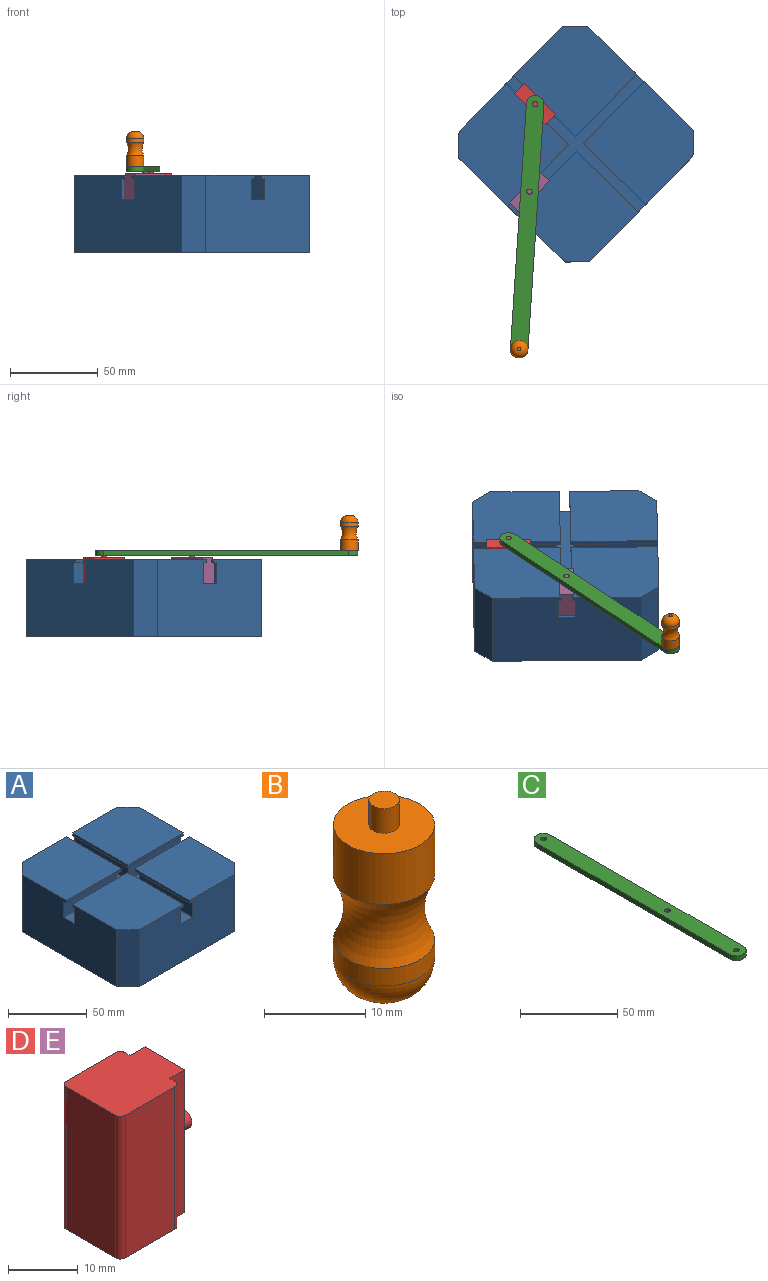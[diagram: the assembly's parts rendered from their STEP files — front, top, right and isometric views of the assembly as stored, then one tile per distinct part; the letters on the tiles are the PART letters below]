
ASSEMBLY  parts=5 mates=5
PART A: 34 faces, bbox 105x105x44 mm
  f0: plane 49.5x49.5mm, normal (0,0,1), area 2400.2mm2, adj f8,f10,f12,f13,f28
  f1: plane 49.5x49.5mm, normal (0,0,1), area 2400.2mm2, adj f4,f5,f10,f11,f33
  f2: plane 49.5x49.5mm, normal (0,0,-1), area 194mm2, adj f4,f5,f6,f10,f31,f33
  f3: plane 49.52x49.5mm, normal (0,0,-1), area 194mm2, adj f13,f15,f23,f25,f26,f29
  f4: plane 85x44mm, normal (1,0,0), area 3608.3mm2, adj f1,f2,f11,f16,f17,f18,f20,f22
  f5: plane 49.5x2mm, normal (-1,0,0), area 99mm2, adj f1,f2,f10,f33
  f6: plane 47.5x12mm, normal (-1,0,0), area 570mm2, adj f2,f10,f22,f31
  f7: plane 47.5x12mm, normal (1,0,0), area 570mm2, adj f10,f22,f24,f27
  f8: plane 49.5x2mm, normal (1,0,0), area 99mm2, adj f0,f10,f24,f28
  f9: plane 49.52x49.5mm, normal (0,0,1), area 2401.5mm2, adj f13,f14,f15,f25,f26
  f10: plane 85x44mm, normal (0,1,0), area 3608mm2, adj f0,f1,f2,f5,f6,f7,f8,f11
  f11: plane 44x10mm, normal (0.71,0.71,0), area 622.3mm2, adj f1,f4,f10,f18
  f12: plane 44x10mm, normal (-0.71,0.71,0), area 622.3mm2, adj f0,f10,f13,f18
  f13: plane 85x44mm, normal (-1,0,0), area 3608.3mm2, adj f0,f3,f9,f12,f14,f18,f22,f24
  f14: plane 44x10mm, normal (-0.71,-0.71,0), area 622.3mm2, adj f9,f13,f15,f18
  f15: plane 85x44mm, normal (0,-1,0), area 3608mm2, adj f3,f9,f14,f16,f17,f18,f19,f20
  f16: plane 44x10mm, normal (0.71,-0.71,0), area 622.3mm2, adj f4,f15,f17,f18
  f17: plane 49.52x49.5mm, normal (0,0,1), area 2401.5mm2, adj f4,f15,f16,f19,f32
  f18: plane 105x105mm, normal (0,0,-1), area 10825mm2, adj f4,f10,f11,f12,f13,f14,f15,f16
  f19: plane 49.52x2mm, normal (-1,0,0), area 99mm2, adj f15,f17,f20,f32
  f20: plane 49.52x49.5mm, normal (0,0,-1), area 194mm2, adj f4,f15,f19,f21,f30,f32
  f21: plane 47.52x12mm, normal (-1,0,0), area 570.3mm2, adj f15,f20,f22,f30
  f22: plane 105x105mm, normal (0,0,1), area 1997.7mm2, adj f4,f6,f7,f10,f13,f15,f21,f23
  f23: plane 47.52x12mm, normal (1,0,0), area 570.3mm2, adj f3,f15,f22,f29
  f24: plane 49.5x49.5mm, normal (0,0,-1), area 194mm2, adj f7,f8,f10,f13,f27,f28
  f25: plane 49.52x2mm, normal (1,0,0), area 99mm2, adj f3,f9,f15,f26
  f26: plane 49.5x2mm, normal (0,1,0), area 99mm2, adj f3,f9,f13,f25
  f27: plane 47.5x12mm, normal (0,-1,0), area 570mm2, adj f7,f13,f22,f24
  f28: plane 49.5x2mm, normal (0,-1,0), area 99mm2, adj f0,f8,f13,f24
  f29: plane 47.5x12mm, normal (0,1,0), area 570mm2, adj f3,f13,f22,f23
  f30: plane 47.5x12mm, normal (0,1,0), area 570mm2, adj f4,f20,f21,f22
  f31: plane 47.5x12mm, normal (0,-1,0), area 570mm2, adj f2,f4,f6,f22
  f32: plane 49.5x2mm, normal (0,1,0), area 99mm2, adj f4,f17,f19,f20
  f33: plane 49.5x2mm, normal (0,-1,0), area 99mm2, adj f1,f2,f4,f5
PART B: 8 faces, bbox 13.7x13.7x23 mm
  f0: plane 2x2mm, normal (0,0,-1), area 3.1mm2, adj f1
  f1: torus R=1mm, axis (0,0,-1), area 140mm2, adj f0,f2
  f2: cylinder r=5mm len=10mm, axis (0,0,-1), area 66.8mm2, adj f1,f3
  f3: torus R=12mm, axis (0,0,-1), area 220.3mm2, adj f2,f4
  f4: cylinder r=5mm len=10mm, axis (0,0,-1), area 192.5mm2, adj f3,f5
  f5: plane 10x10mm, normal (0,0,1), area 71.5mm2, adj f4,f6
  f6: cylinder r=1.5mm len=3mm, axis (0,0,-1), area 28.3mm2, adj f5,f7
  f7: plane 3x3mm, normal (0,0,1), area 7.1mm2, adj f6
PART C: 9 faces, bbox 10x150x3 mm
  f0: cylinder r=5mm len=10mm, axis (0,0,-1), area 47.1mm2, adj f1,f6,f7,f8
  f1: plane 140x3mm, normal (-1,0,0), area 420mm2, adj f0,f2,f7,f8
  f2: cylinder r=5mm len=10mm, axis (0,0,-1), area 47.1mm2, adj f1,f6,f7,f8
  f3: cylinder r=1.5mm len=3mm, axis (0,0,-1), area 28.3mm2, adj f7,f8
  f4: cylinder r=1.5mm len=3mm, axis (0,0,-1), area 28.3mm2, adj f7,f8
  f5: cylinder r=1.5mm len=3mm, axis (0,0,-1), area 28.3mm2, adj f7,f8
  f6: plane 140x3mm, normal (1,0,0), area 420mm2, adj f0,f2,f7,f8
  f7: plane 150x10mm, normal (0,0,1), area 1457.3mm2, adj f0,f1,f2,f3,f4,f5,f6
  f8: plane 150x10mm, normal (0,0,-1), area 1457.3mm2, adj f0,f1,f2,f3,f4,f5,f6
PART D: 16 faces, bbox 19x12x25 mm
  f0: plane 25x1mm, normal (1,0,0), area 25mm2, adj f1,f3,f8,f13
  f1: plane 15x12mm, normal (0,0,-1), area 167.1mm2, adj f0,f2,f4,f5,f6,f7,f8,f9
  f2: plane 25x10mm, normal (0,1,0), area 250mm2, adj f1,f3,f13,f14
  f3: plane 15x12mm, normal (0,0,1), area 167.1mm2, adj f0,f2,f4,f5,f6,f7,f8,f9
  f4: plane 25x10mm, normal (0,-1,0), area 250mm2, adj f1,f3,f12,f15
  f5: plane 25x1mm, normal (1,0,0), area 25mm2, adj f1,f3,f7,f12
  f6: plane 25x10mm, normal (-1,0,0), area 250mm2, adj f1,f3,f14,f15
  f7: plane 25x3mm, normal (0,-1,0), area 75mm2, adj f1,f3,f5,f9
  f8: plane 25x3mm, normal (0,1,0), area 75mm2, adj f0,f1,f3,f9
  f9: plane 25x8mm, normal (1,0,0), area 192.9mm2, adj f1,f3,f7,f8,f10
  f10: cylinder r=1.5mm len=4mm, axis (-1,0,0), area 37.7mm2, adj f9,f11
  f11: plane 3x3mm, normal (1,0,0), area 7.1mm2, adj f10
  f12: cylinder r=1mm len=25mm, axis (0,0,1), area 39.3mm2, adj f1,f3,f4,f5
  f13: cylinder r=1mm len=25mm, axis (0,0,-1), area 39.3mm2, adj f0,f1,f2,f3
  f14: cylinder r=1mm len=25mm, axis (0,0,1), area 39.3mm2, adj f1,f2,f3,f6
  f15: cylinder r=1mm len=25mm, axis (0,0,-1), area 39.3mm2, adj f1,f3,f4,f6
PART E: same geometry as D
PLACE A rot(axis=(0,0,-1),134.3deg) t=(-66.8,1.1,-30)mm fixed
PLACE B rot(axis=(0.68,-0.73,0),180deg) t=(39.52,-119.17,78.07)mm
PLACE C rot(axis=(0,0,1),176.3deg) t=(51.57,20.34,15.92)mm
PLACE D rot(axis=(-0.35,-0.87,-0.35),98.2deg) t=(49.82,74.19,-0.08)mm
PLACE E rot(axis=(-0.68,-0.29,-0.68),148.1deg) t=(30.39,-90.8,-0.08)mm
MATE fastened C.f0 <-> B.f1  axis (0,0,-1) through (-24.93,-114.97,15.92)mm
MATE revolute C.f5 <-> E.f10  axis (0,0,1) through (-19.07,-25.16,18.92)mm
MATE revolute C.f2 <-> D.f10  axis (0,0,1) through (-15.82,24.73,18.92)mm
MATE slider D.f3 <-> A.f10  axis (-0.72,0.7,0) through (-24.77,33.46,7)mm
MATE slider E.f3 <-> A.f4  axis (0.7,0.72,0) through (-10.35,-16.21,7)mm
